# Revit family: Скамейка стальная «Лондон» Арт 14839
name_source: partatom
category: Антураж
revit_build: Autodesk Revit 2018 (Build: 20180423_1000(x64)
units: mm (PartAtom-declared; Revit-internal decimal feet)

## family parameters
Всегда вертикально = Да
Источник визуального образа = Геометрия семейства
На основе рабочей плоскости = Нет
Общий = Нет
При загрузке вырезать с полостями = Нет
Точка расчета площади = Нет

## types (4) — shared parameters
URL = https://hobbyka.ru
Артикул товара = Арт. 14839
Высота = 775 мм
Группа модели = Скамейки
Изготовитель = ООО «Хоббика»
Изображение типоразмера = Скамейка стальная «Лондон» Арт 14839.jpg
Материал изделия = Дерево, сталь
Цвет каркаса = Сталь
Цвет лавки = Орех
Ширина = 600 мм

## per-type parameters (varying)
| type | 4 опоры | Версия 2,0 м | Версия 3,0 м | Версия 4,5 м | Версия 6,0 м | Длина | Описание |
| Версия 2,0 м | Нет | Да | Нет | Нет | Нет | 2000 мм | Скамейка стальная «Лондон». Версия 2,0 м |
| Версия 3,0 м | Нет | Нет | Да | Нет | Нет | 3000 мм | Скамейка стальная «Лондон». Версия 3,0 м |
| Версия 4,5 м | Да | Нет | Нет | Да | Нет | 4500 мм | Скамейка стальная «Лондон». Версия 4,5 м |
| Версия 6,0 м | Да | Нет | Нет | Нет | Да | 6000 мм | Скамейка стальная «Лондон». Версия 6,0 м |

## geometry (parser evidence)
native form markers: Blend x2
no freeform markers — native parametric forms only
